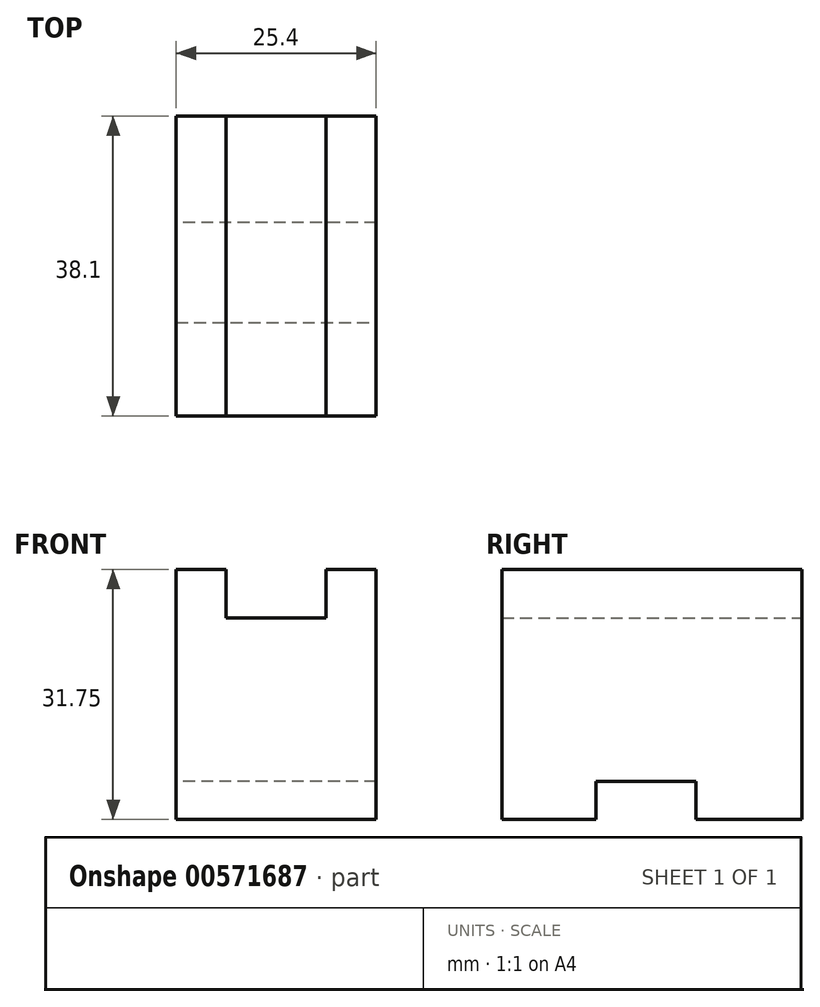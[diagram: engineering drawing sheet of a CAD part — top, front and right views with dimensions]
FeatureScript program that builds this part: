
annotation { "Feature Type Name" : "Feature", "Feature Type Description" : "" }
export const myFeature = defineFeature(function(context is Context, id is Id, definition is map)
    precondition{}
    {
        {
            var Q0;
            Q0=qCreatedBy(makeId("Front.planeOp"),FACE);
            var sketch = newSketch(context, id + "F0", { "sketchPlane" : qUnion([Q0])});
            skLineSegment(sketch, "E0", {"start": v(-56.13, 54.06) * mm, "end": v(-56.13, 22.3) * mm});
            skLineSegment(sketch, "E1", {"start": v(-56.13, 22.3) * mm, "end": v(-30.73, 22.3) * mm});
            skLineSegment(sketch, "E2", {"start": v(-30.73, 22.3) * mm, "end": v(-30.73, 54.06) * mm});
            skLineSegment(sketch, "E3", {"start": v(-56.13, 54.06) * mm, "end": v(-49.78, 54.06) * mm});
            skLineSegment(sketch, "E4", {"start": v(-49.78, 54.06) * mm, "end": v(-49.78, 47.93) * mm});
            skLineSegment(sketch, "E5", {"start": v(-49.78, 47.93) * mm, "end": v(-37.08, 47.93) * mm});
            skLineSegment(sketch, "E6", {"start": v(-37.08, 47.93) * mm, "end": v(-37.08, 54.06) * mm});
            skLineSegment(sketch, "E7", {"start": v(-37.08, 54.06) * mm, "end": v(-30.73, 54.06) * mm});
            skSolve(sketch);
        }
        {
            var Q0;
            Q0 = qSketchRegion(id + "F0", true);
            extrude(context, id + "F1", {"entities" : qUnion([Q0]), "depth" : 38.1 * mm, "offsetDistance" : 25.4 * mm});
        }
        {
            var Q0;
            Q0=makeQuery(id+"F1.opExtrude","SWEPT_FACE",FACE,{"disambiguationData":[OSD([sQuery(id+"F0.wireOp",EDGE,"E0")])]});
            var sketch = newSketch(context, id + "F2", { "sketchPlane" : qUnion([Q0])});
            skLineSegment(sketch, "E8", {"start": v(13.5, 27.17) * mm, "end": v(13.5, 20.82) * mm});
            skLineSegment(sketch, "E9", {"start": v(13.5, 20.82) * mm, "end": v(26.2, 20.82) * mm});
            skLineSegment(sketch, "E10", {"start": v(26.2, 20.82) * mm, "end": v(26.2, 27.17) * mm});
            skLineSegment(sketch, "E11", {"start": v(26.2, 27.17) * mm, "end": v(13.5, 27.17) * mm});
            skSolve(sketch);
        }
        {
            var Q0;
            Q0 = qSketchRegion(id + "F2", true);
            extrude(context, id + "F3", {"entities" : qUnion([Q0]), "operationType" : NewBodyOperationType.REMOVE, "oppositeDirection" : true, "depth" : 25.4 * mm, "offsetDistance" : 25.4 * mm});
        }
    });
